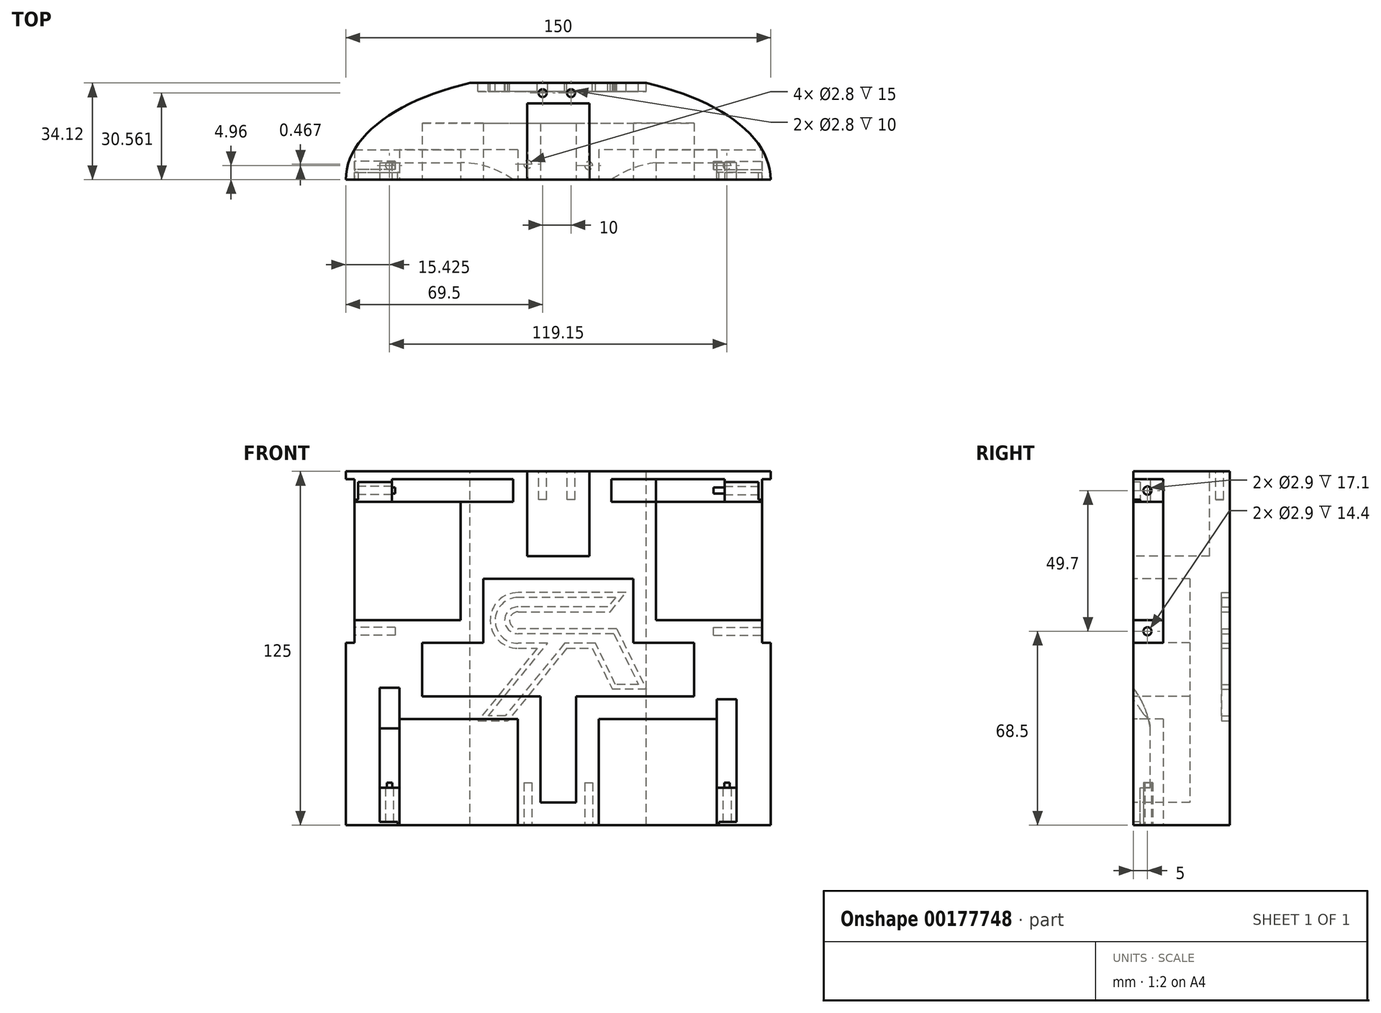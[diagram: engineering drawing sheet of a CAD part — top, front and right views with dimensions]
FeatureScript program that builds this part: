
annotation { "Feature Type Name" : "Feature", "Feature Type Description" : "" }
export const myFeature = defineFeature(function(context is Context, id is Id, definition is map)
    precondition{}
    {
        {
            var Q0;
            Q0=qCreatedBy(makeId("Top.planeOp"),FACE);
            var sketch = newSketch(context, id + "F0", { "sketchPlane" : qUnion([Q0])});
            skLineSegment(sketch, "E0.bottom", {"start": v(-150, 0) * mm, "end": v(0, 0) * mm});
            skLineSegment(sketch, "E0.top", {"start": v(-150, -75) * mm, "end": v(0, -75) * mm});
            skLineSegment(sketch, "E0.left", {"start": v(-150, 0) * mm, "end": v(-150, -75) * mm});
            skLineSegment(sketch, "E0.right", {"start": v(0, 0) * mm, "end": v(0, -75) * mm});
            skLineSegment(sketch, "E1", {"start": v(0, -37.5) * mm, "end": v(-150, -37.5) * mm});
            skPoint(sketch, "E2", {"position": v(-75, -37.5) * mm});
            skEllipse(sketch, "E3", {"center": v(-75, -37.5) * mm, "majorRadius": 75 * mm, "minorRadius": 37.5 * mm, "majorAxis": v(1, 0)});
            skSolve(sketch);
        }
        {
            var Q0;
            {var subQ0=sQuery(id+"F0.wireOp",EDGE,"E1");Q0=makeQuery(id+"F0.imprint","IMPRINT",FACE,{"disambiguationData":[TD([[makeQuery(id+"F0.imprint","IMPRINT",EDGE,{"derivedFrom":subQ0}),1.0]])]});}
            var Q1;
            {var subQ0=sQuery(id+"F0.wireOp",EDGE,"E1");Q1=makeQuery(id+"F0.imprint","IMPRINT",FACE,{"disambiguationData":[TD([[makeQuery(id+"F0.imprint","IMPRINT",EDGE,{"derivedFrom":subQ0}),-1.0]])]});}
            extrude(context, id + "F1", {"entities" : qUnion([Q0, Q1]), "depth" : 125 * mm});
        }
        {
            var Q0;
            Q0=qCreatedBy(makeId("Right.planeOp"),FACE);
            var sketch = newSketch(context, id + "F2", { "sketchPlane" : qUnion([Q0])});
            skLineSegment(sketch, "E4.bottom", {"start": v(-48.1, 114.2) * mm, "end": v(-26.9, 114.2) * mm});
            skLineSegment(sketch, "E4.top", {"start": v(-48.1, 72.5) * mm, "end": v(-26.9, 72.5) * mm});
            skLineSegment(sketch, "E4.left", {"start": v(-48.1, 114.2) * mm, "end": v(-48.1, 72.5) * mm});
            skLineSegment(sketch, "E4.right", {"start": v(-26.9, 114.2) * mm, "end": v(-26.9, 72.5) * mm});
            skPoint(sketch, "E5", {"position": v(-37.5, 125) * mm});
            skPoint(sketch, "E6", {"position": v(-37.5, 114.2) * mm});
            skLineSegment(sketch, "E7", {"start": v(-37.5, 125) * mm, "end": v(-37.5, 121.35) * mm});
            skLineSegment(sketch, "E8.bottom", {"start": v(-48.1, 113.35) * mm, "end": v(-26.9, 113.35) * mm, "construction": true});
            skLineSegment(sketch, "E8.top", {"start": v(-48.1, 73.35) * mm, "end": v(-26.9, 73.35) * mm, "construction": true});
            skLineSegment(sketch, "E8.left", {"start": v(-48.1, 113.35) * mm, "end": v(-48.1, 73.35) * mm, "construction": true});
            skLineSegment(sketch, "E8.right", {"start": v(-26.9, 113.35) * mm, "end": v(-26.9, 73.35) * mm, "construction": true});
            skPoint(sketch, "E9", {"position": v(-26.9, 93.35) * mm});
            skLineSegment(sketch, "E10.bottom", {"start": v(-48.1, 113.35) * mm, "end": v(-26.9, 113.35) * mm});
            skLineSegment(sketch, "E10.top", {"start": v(-48.1, 121.35) * mm, "end": v(-26.9, 121.35) * mm});
            skLineSegment(sketch, "E10.left", {"start": v(-48.1, 113.35) * mm, "end": v(-48.1, 121.35) * mm});
            skLineSegment(sketch, "E10.right", {"start": v(-26.9, 113.35) * mm, "end": v(-26.9, 121.35) * mm});
            skLineSegment(sketch, "E11.bottom", {"start": v(-48.1, 73.35) * mm, "end": v(-26.9, 73.35) * mm});
            skLineSegment(sketch, "E11.top", {"start": v(-48.1, 65.35) * mm, "end": v(-26.9, 65.35) * mm});
            skLineSegment(sketch, "E11.left", {"start": v(-48.1, 73.35) * mm, "end": v(-48.1, 65.35) * mm});
            skLineSegment(sketch, "E11.right", {"start": v(-26.9, 73.35) * mm, "end": v(-26.9, 65.35) * mm});
            skLineSegment(sketch, "E12", {"start": v(-37.5, 65.35) * mm, "end": v(-37.5, 0) * mm});
            skLineSegment(sketch, "E13", {"start": v(-37.5, 121.35) * mm, "end": v(-37.5, 125) * mm});
            skLineSegment(sketch, "E14.trimOffspring", {"start": v(-37.5, 114.2) * mm, "end": v(-37.5, 72.5) * mm});
            skSolve(sketch);
        }
        {
            var Q0;
            {var subQ0=sQuery(id+"F2.wireOp",EDGE,"E4.right");Q0=makeQuery(id+"F2.imprint","IMPRINT",FACE,{"disambiguationData":[TD([[makeQuery(id+"F2.imprint","IMPRINT",EDGE,{"derivedFrom":subQ0}),-1.0]])]});}
            var Q1;
            {var subQ0=sQuery(id+"F2.wireOp",EDGE,"E4.left");Q1=makeQuery(id+"F2.imprint","IMPRINT",FACE,{"disambiguationData":[TD([[makeQuery(id+"F2.imprint","IMPRINT",EDGE,{"derivedFrom":subQ0}),1.0]])]});}
            var Q2;
            {var subQ0=sQuery(id+"F2.wireOp",EDGE,"E11.left");var subQ1=sQuery(id+"F2.wireOp",EDGE,"E4.top");var subQ2=makeQuery(id+"F2.imprint","INTERSECT",VERTEX,{"derivedFrom":[subQ1,subQ0]});Q2=makeQuery(id+"F2.imprint","IMPRINT",FACE,{"disambiguationData":[TD([[makeQuery(id+"F2.imprint","IMPRINT",EDGE,{"disambiguationData":[TD([[subQ2,-1.0]])],"derivedFrom":subQ1}),1.0]])]});}
            var Q3;
            {var subQ0=sQuery(id+"F2.wireOp",EDGE,"E11.right");var subQ1=sQuery(id+"F2.wireOp",EDGE,"E4.top");var subQ2=makeQuery(id+"F2.imprint","INTERSECT",VERTEX,{"derivedFrom":[subQ1,subQ0]});Q3=makeQuery(id+"F2.imprint","IMPRINT",FACE,{"disambiguationData":[TD([[makeQuery(id+"F2.imprint","IMPRINT",EDGE,{"disambiguationData":[TD([[subQ2,1.0]])],"derivedFrom":subQ1}),1.0]])]});}
            var Q4;
            {var subQ0=sQuery(id+"F2.wireOp",EDGE,"E10.left");var subQ1=sQuery(id+"F2.wireOp",EDGE,"E4.bottom");var subQ2=makeQuery(id+"F2.imprint","INTERSECT",VERTEX,{"derivedFrom":[subQ1,subQ0]});Q4=makeQuery(id+"F2.imprint","IMPRINT",FACE,{"disambiguationData":[TD([[makeQuery(id+"F2.imprint","IMPRINT",EDGE,{"disambiguationData":[TD([[subQ2,-1.0]])],"derivedFrom":subQ1}),-1.0]])]});}
            var Q5;
            {var subQ0=sQuery(id+"F2.wireOp",EDGE,"E10.right");var subQ1=sQuery(id+"F2.wireOp",EDGE,"E4.bottom");var subQ2=makeQuery(id+"F2.imprint","INTERSECT",VERTEX,{"derivedFrom":[subQ1,subQ0]});Q5=makeQuery(id+"F2.imprint","IMPRINT",FACE,{"disambiguationData":[TD([[makeQuery(id+"F2.imprint","IMPRINT",EDGE,{"disambiguationData":[TD([[subQ2,1.0]])],"derivedFrom":subQ1}),-1.0]])]});}
            extrude(context, id + "F3", {"entities" : qUnion([Q0, Q1, Q2, Q3, Q4, Q5]), "operationType" : NewBodyOperationType.REMOVE, "oppositeDirection" : true, "depth" : 155.5 * mm});
        }
        {
            var Q0;
            Q0=makeQuery(id+"F3.boolean.opBoolean","COPY",FACE,{"derivedFrom":makeQuery(id+"F3.opExtrude","SWEPT_FACE",FACE,{"disambiguationData":[OSD([sQuery(id+"F2.wireOp",EDGE,"E4.top")])]})});
            var sketch = newSketch(context, id + "F4", { "sketchPlane" : qUnion([Q0])});
            skLineSegment(sketch, "E15", {"start": v(-3.06, -48.1) * mm, "end": v(-3.06, -26.9) * mm});
            skEllipticalArc(sketch, "E16.0", {});
            skLineSegment(sketch, "E17", {"start": v(-146.94, -48.1) * mm, "end": v(-146.94, -26.9) * mm});
            skEllipticalArc(sketch, "E18.0", {});
            const initialGuessF4  = {"E16.0": [-0.075, -0.0375, 1, 0, 0.075, 0.0375, 5.996612290444908, 0.28657301673467844], "E18.0": [-0.075, -0.0375, 1, 0, 0.075, 0.0375, 2.855019636855115, 3.428165670324471]};
            skSetInitialGuess(sketch, initialGuessF4);
            skSolve(sketch);
        }
        {
            var Q0;
            Q0=makeQuery(id+"F4.imprint","IMPRINT",FACE,{"disambiguationData":[TD([[makeQuery(id+"F4.imprint","IMPRINT",EDGE,{"derivedFrom":sQuery(id+"F4.wireOp",EDGE,"E17")}),1.0]])]});
            var Q1;
            Q1=makeQuery(id+"F4.imprint","IMPRINT",FACE,{"disambiguationData":[TD([[makeQuery(id+"F4.imprint","IMPRINT",EDGE,{"derivedFrom":sQuery(id+"F4.wireOp",EDGE,"E15")}),-1.0]])]});
            extrude(context, id + "F5", {"entities" : qUnion([Q0, Q1]), "operationType" : NewBodyOperationType.REMOVE, "oppositeDirection" : true, "depth" : 8 * mm});
        }
        {
            var Q0;
            Q0=makeQuery(id+"F3.boolean.opBoolean","COPY",FACE,{"derivedFrom":makeQuery(id+"F3.opExtrude","SWEPT_FACE",FACE,{"disambiguationData":[OSD([sQuery(id+"F2.wireOp",EDGE,"E4.bottom")])]})});
            var sketch = newSketch(context, id + "F6", { "sketchPlane" : qUnion([Q0])});
            skLineSegment(sketch, "E19", {"start": v(-3.06, 26.9) * mm, "end": v(-3.06, 48.1) * mm});
            skEllipticalArc(sketch, "E20.0", {});
            skLineSegment(sketch, "E21", {"start": v(-146.94, 26.9) * mm, "end": v(-146.94, 48.1) * mm});
            skEllipticalArc(sketch, "E22.0", {});
            const initialGuessF6  = {"E20.0": [-0.075, 0.0375, 1, 0, 0.075, 0.0375, 5.996612290444908, 0.28657301673467805], "E22.0": [-0.075, 0.0375, 1, 0, 0.075, 0.0375, 2.8550196368551153, 3.428165670324471]};
            skSetInitialGuess(sketch, initialGuessF6);
            skSolve(sketch);
        }
        {
            var Q0;
            Q0=makeQuery(id+"F6.imprint","IMPRINT",FACE,{"disambiguationData":[TD([[makeQuery(id+"F6.imprint","IMPRINT",EDGE,{"derivedFrom":sQuery(id+"F6.wireOp",EDGE,"E21")}),1.0]])]});
            var Q1;
            Q1=makeQuery(id+"F6.imprint","IMPRINT",FACE,{"disambiguationData":[TD([[makeQuery(id+"F6.imprint","IMPRINT",EDGE,{"derivedFrom":sQuery(id+"F6.wireOp",EDGE,"E19")}),-1.0]])]});
            extrude(context, id + "F7", {"entities" : qUnion([Q0, Q1]), "operationType" : NewBodyOperationType.REMOVE, "oppositeDirection" : true, "depth" : 8 * mm});
        }
        {
            var Q0;
            Q0=makeQuery(id+"F3.boolean.opBoolean","COPY",FACE,{"derivedFrom":makeQuery(id+"F3.opExtrude","SWEPT_FACE",FACE,{"disambiguationData":[OSD([sQuery(id+"F2.wireOp",EDGE,"E4.top")])]})});
            var sketch = newSketch(context, id + "F8", { "sketchPlane" : qUnion([Q0])});
            skLineSegment(sketch, "E23.bottom", {"start": v(-109.44, -26.9) * mm, "end": v(-40.56, -26.9) * mm});
            skLineSegment(sketch, "E23.top", {"start": v(-109.44, -48.1) * mm, "end": v(-40.56, -48.1) * mm});
            skLineSegment(sketch, "E23.left", {"start": v(-109.44, -26.9) * mm, "end": v(-109.44, -48.1) * mm});
            skLineSegment(sketch, "E23.right", {"start": v(-40.56, -26.9) * mm, "end": v(-40.56, -48.1) * mm});
            skSolve(sketch);
        }
        {
            var Q0;
            Q0=makeQuery(id+"F8.imprint","IMPRINT",FACE,{"disambiguationData":[TD([[makeQuery(id+"F8.imprint","IMPRINT",EDGE,{"derivedFrom":sQuery(id+"F8.wireOp",EDGE,"E23.bottom")}),-1.0]])]});
            extrude(context, id + "F9", {"entities" : qUnion([Q0]), "operationType" : NewBodyOperationType.ADD, "depth" : 46 * mm});
        }
        {
            var Q0;
            Q0=makeQuery(id+"F9.boolean.opBoolean","SPLIT",FACE,{"disambiguationData":[TD([makeQuery(id+"F7.boolean.opBoolean","COPY",FACE,{"derivedFrom":makeQuery(id+"F7.opExtrude","SWEPT_FACE",FACE,{"disambiguationData":[OSD([sQuery(id+"F6.wireOp",EDGE,"E21")])]})})])],"derivedFrom":makeQuery(id+"F3.boolean.opBoolean","COPY",FACE,{"derivedFrom":makeQuery(id+"F3.opExtrude","SWEPT_FACE",FACE,{"disambiguationData":[OSD([sQuery(id+"F2.wireOp",EDGE,"E4.bottom")])]})})});
            var sketch = newSketch(context, id + "F10", { "sketchPlane" : qUnion([Q0])});
            skLineSegment(sketch, "E24", {"start": v(-145.7, 26.9) * mm, "end": v(-145.7, 48.1) * mm, "construction": true});
            skLineSegment(sketch, "E25", {"start": v(-145.7, 37.5) * mm, "end": v(-142.91, 37.5) * mm});
            skLineSegment(sketch, "E26.bottom", {"start": v(-145.7, 35) * mm, "end": v(-4.3, 35) * mm});
            skLineSegment(sketch, "E26.top", {"start": v(-145.7, 40) * mm, "end": v(-4.3, 40) * mm});
            skLineSegment(sketch, "E26.left", {"start": v(-145.7, 35) * mm, "end": v(-145.7, 40) * mm});
            skLineSegment(sketch, "E26.right", {"start": v(-4.3, 35) * mm, "end": v(-4.3, 40) * mm});
            skLineSegment(sketch, "E27", {"start": v(-4.3, 26.9) * mm, "end": v(-4.3, 48.1) * mm, "construction": true});
            skLineSegment(sketch, "E28", {"start": v(-145.7, 37.5) * mm, "end": v(-145.7, 40) * mm});
            skLineSegment(sketch, "E29", {"start": v(-145.7, 35) * mm, "end": v(-145.7, 37.5) * mm});
            skSolve(sketch);
        }
        {
            var Q0;
            Q0=qSketchRegion(id+"F10",true);
            extrude(context, id + "F11", {"entities" : qUnion([Q0]), "operationType" : NewBodyOperationType.REMOVE, "oppositeDirection" : true, "depth" : 7 * mm});
        }
        {
            var Q0;
            Q0=makeQuery(id+"F9.boolean.opBoolean","SPLIT",FACE,{"disambiguationData":[TD([makeQuery(id+"F7.boolean.opBoolean","COPY",FACE,{"derivedFrom":makeQuery(id+"F7.opExtrude","SWEPT_FACE",FACE,{"disambiguationData":[OSD([sQuery(id+"F6.wireOp",EDGE,"E21")])]})})])],"derivedFrom":makeQuery(id+"F3.boolean.opBoolean","COPY",FACE,{"derivedFrom":makeQuery(id+"F3.opExtrude","SWEPT_FACE",FACE,{"disambiguationData":[OSD([sQuery(id+"F2.wireOp",EDGE,"E4.bottom")])]})})});
            var sketch = newSketch(context, id + "F12", { "sketchPlane" : qUnion([Q0])});
            skLineSegment(sketch, "E30.bottom", {"start": v(-133.7, 31.5) * mm, "end": v(-16.3, 31.5) * mm});
            skLineSegment(sketch, "E30.top", {"start": v(-133.7, 43.5) * mm, "end": v(-16.3, 43.5) * mm});
            skLineSegment(sketch, "E30.left", {"start": v(-133.7, 31.5) * mm, "end": v(-133.7, 43.5) * mm});
            skLineSegment(sketch, "E30.right", {"start": v(-16.3, 31.5) * mm, "end": v(-16.3, 43.5) * mm});
            skLineSegment(sketch, "E31", {"start": v(-133.7, 35) * mm, "end": v(-133.7, 40) * mm});
            skPoint(sketch, "E32", {"position": v(-133.7, 37.5) * mm});
            skLineSegment(sketch, "E33", {"start": v(-16.3, 35) * mm, "end": v(-16.3, 40) * mm});
            skPoint(sketch, "E34", {"position": v(-16.3, 37.5) * mm});
            skSolve(sketch);
        }
        {
            var Q0;
            Q0=qSketchRegion(id+"F12",true);
            extrude(context, id + "F13", {"entities" : qUnion([Q0]), "operationType" : NewBodyOperationType.REMOVE, "oppositeDirection" : true, "depth" : 8 * mm});
        }
        {
            var Q0;
            Q0=makeQuery(id+"F9.boolean.opBoolean","SPLIT",FACE,{"disambiguationData":[TD([makeQuery(id+"F7.boolean.opBoolean","COPY",FACE,{"derivedFrom":makeQuery(id+"F7.opExtrude","SWEPT_FACE",FACE,{"disambiguationData":[OSD([sQuery(id+"F6.wireOp",EDGE,"E21")])]})})])],"derivedFrom":makeQuery(id+"F3.boolean.opBoolean","COPY",FACE,{"derivedFrom":makeQuery(id+"F3.opExtrude","SWEPT_FACE",FACE,{"disambiguationData":[OSD([sQuery(id+"F2.wireOp",EDGE,"E4.bottom")])]})})});
            var sketch = newSketch(context, id + "F14", { "sketchPlane" : qUnion([Q0])});
            skArc(sketch, "E35", {"start": v(-109.44, 31.5) * mm, "mid": v(-83.34, 45.45) * mm, "end": v(-80.45, 74.9) * mm});
            skArc(sketch, "E36", {"start": v(-109.44, 43.5) * mm, "mid": v(-91.99, 53.74) * mm, "end": v(-92.41, 73.98) * mm});
            skEllipticalArc(sketch, "E37.0", {});
            skLineSegment(sketch, "E38", {"start": v(-109.44, 31.5) * mm, "end": v(-109.44, 43.5) * mm});
            skArc(sketch, "E39", {"start": v(-69.55, 74.9) * mm, "mid": v(-65.03, 46.53) * mm, "end": v(-40.56, 31.5) * mm});
            skArc(sketch, "E40", {"start": v(-57.59, 73.98) * mm, "mid": v(-55.43, 55.19) * mm, "end": v(-40.56, 43.5) * mm});
            skEllipticalArc(sketch, "E41.0", {});
            skLineSegment(sketch, "E42", {"start": v(-40.56, 31.5) * mm, "end": v(-40.56, 43.5) * mm});
            skLineSegment(sketch, "E43", {"start": v(-75, 37.5) * mm, "end": v(-75, 74.9) * mm, "construction": true});
            skLineSegment(sketch, "E44", {"start": v(-69.55, 74.9) * mm, "end": v(-75, 74.9) * mm, "construction": true});
            skLineSegment(sketch, "E45", {"start": v(-80.45, 74.9) * mm, "end": v(-75, 74.9) * mm, "construction": true});
            const initialGuessF14  = {"E37.0": [-0.075, 0.0375, 1, 0, 0.075, 0.0375, 1.6434997456011395, 1.8050969396186902], "E41.0": [-0.075, 0.0375, 1, 0, 0.075, 0.0375, 1.3364957139711027, 1.4980929079886538], "E37.0": [-0.075, 0.0375, 1, 0, 0.075, 0.0375, 1.6434997456011395, 1.8050969396186902]};
            skSetInitialGuess(sketch, initialGuessF14);
            skSolve(sketch);
        }
        {
            var Q0;
            Q0=qSketchRegion(id+"F14",true);
            extrude(context, id + "F15", {"entities" : qUnion([Q0]), "operationType" : NewBodyOperationType.REMOVE, "oppositeDirection" : true, "depth" : 8 * mm});
        }
        {
            var Q0;
            Q0=makeQuery(id+"F15.boolean.opBoolean","MERGE",FACE,{"derivedFrom":[makeQuery(id+"F13.boolean.opBoolean","MERGE",FACE,{"derivedFrom":[makeQuery(id+"F11.boolean.opBoolean","COPY",FACE,{"derivedFrom":makeQuery(id+"F11.opExtrude","CAP_FACE",FACE,{"disambiguationData":[OSD([sQuery(id+"F10.wireOp",EDGE,"E26.bottom"),sQuery(id+"F10.wireOp",EDGE,"E26.top"),sQuery(id+"F10.wireOp",EDGE,"E26.right"),sQuery(id+"F10.wireOp",EDGE,"E28"),sQuery(id+"F10.wireOp",EDGE,"E29")])],"isStart":true})}),makeQuery(id+"F13.opExtrude","CAP_FACE",FACE,{"disambiguationData":[OSD([sQuery(id+"F12.wireOp",EDGE,"E30.bottom"),sQuery(id+"F12.wireOp",EDGE,"E30.top"),sQuery(id+"F12.wireOp",EDGE,"E30.left"),sQuery(id+"F12.wireOp",EDGE,"E30.right"),sQuery(id+"F12.wireOp",EDGE,"E31"),sQuery(id+"F12.wireOp",EDGE,"E33")])],"isStart":true})]}),makeQuery(id+"F15.opExtrude","CAP_FACE",FACE,{"disambiguationData":[OSD([sQuery(id+"F14.wireOp",EDGE,"E35"),sQuery(id+"F14.wireOp",EDGE,"E36"),sQuery(id+"F14.wireOp",EDGE,"E38"),sQuery(id+"F14.wireOp",EDGE,"E37.0")])],"isStart":true}),makeQuery(id+"F15.opExtrude","CAP_FACE",FACE,{"disambiguationData":[OSD([sQuery(id+"F14.wireOp",EDGE,"E39"),sQuery(id+"F14.wireOp",EDGE,"E40"),sQuery(id+"F14.wireOp",EDGE,"E41.0"),sQuery(id+"F14.wireOp",EDGE,"E42")])],"isStart":true})]});
            var sketch = newSketch(context, id + "F16", { "sketchPlane" : qUnion([Q0])});
            skArc(sketch, "E46.0", {"start": v(-84.76, -43.5) * mm, "mid": v(-78.35, -58.62) * mm, "end": v(-80.45, -74.9) * mm, "construction": true});
            skArc(sketch, "E46.1", {"start": v(-69.55, -74.9) * mm, "mid": v(-70.05, -58.36) * mm, "end": v(-62.76, -43.5) * mm, "construction": true});
            skLineSegment(sketch, "E47", {"start": v(-62.76, -43.5) * mm, "end": v(-84.76, -43.5) * mm});
            skArc(sketch, "E48", {"start": v(-84.76, -43.5) * mm, "mid": v(-95.72, -34.66) * mm, "end": v(-109.44, -31.5) * mm});
            skArc(sketch, "E49", {"start": v(-40.56, -31.5) * mm, "mid": v(-52.8, -35.39) * mm, "end": v(-62.76, -43.5) * mm});
            skLineSegment(sketch, "E50", {"start": v(-109.44, -31.5) * mm, "end": v(-40.56, -31.5) * mm});
            skSolve(sketch);
        }
        {
            var Q0;
            Q0=qSketchRegion(id+"F16",true);
            extrude(context, id + "F17", {"entities" : qUnion([Q0]), "operationType" : NewBodyOperationType.ADD, "depth" : 9.4 * mm});
        }
        {
            var Q0;
            Q0=makeQuery(id+"F7.boolean.opBoolean","COPY",FACE,{"derivedFrom":makeQuery(id+"F7.opExtrude","SWEPT_FACE",FACE,{"disambiguationData":[OSD([sQuery(id+"F6.wireOp",EDGE,"E19")])]})});
            var sketch = newSketch(context, id + "F18", { "sketchPlane" : qUnion([Q0])});
            skLineSegment(sketch, "E51", {"start": v(-48.1, 118.2) * mm, "end": v(-26.9, 118.2) * mm, "construction": true});
            skCircle(sketch, "E52", {"center": v(-42.5, 118.2) * mm, "radius": 1.45 * mm});
            skCircle(sketch, "E53", {"center": v(-32.5, 118.2) * mm, "radius": 1.45 * mm});
            skLineSegment(sketch, "E54", {"start": v(-32.5, 118.2) * mm, "end": v(-42.5, 118.2) * mm});
            skPoint(sketch, "E55", {"position": v(-37.5, 118.2) * mm});
            skLineSegment(sketch, "E56", {"start": v(-26.9, 68.5) * mm, "end": v(-48.1, 68.5) * mm, "construction": true});
            skCircle(sketch, "E57", {"center": v(-32.5, 68.5) * mm, "radius": 1.45 * mm});
            skCircle(sketch, "E58", {"center": v(-42.5, 68.5) * mm, "radius": 1.45 * mm});
            skPoint(sketch, "E59", {"position": v(-37.5, 68.5) * mm});
            skLineSegment(sketch, "E60", {"start": v(-32.5, 68.5) * mm, "end": v(-42.5, 68.5) * mm});
            skSolve(sketch);
        }
        {
            var Q0;
            Q0=qSketchRegion(id+"F18",true);
            extrude(context, id + "F19", {"entities" : qUnion([Q0]), "operationType" : NewBodyOperationType.REMOVE, "oppositeDirection" : true, "depth" : 17.1 * mm});
        }
        {
            var Q0;
            Q0=makeQuery(id+"F7.boolean.opBoolean","COPY",FACE,{"derivedFrom":makeQuery(id+"F7.opExtrude","SWEPT_FACE",FACE,{"disambiguationData":[OSD([sQuery(id+"F6.wireOp",EDGE,"E21")])]})});
            var sketch = newSketch(context, id + "F20", { "sketchPlane" : qUnion([Q0])});
            skCircle(sketch, "E61.0", {"center": v(32.5, 68.5) * mm, "radius": 1.45 * mm});
            skCircle(sketch, "E61.1", {"center": v(42.5, 68.5) * mm, "radius": 1.45 * mm});
            skCircle(sketch, "E61.2", {"center": v(42.5, 118.2) * mm, "radius": 1.45 * mm});
            skCircle(sketch, "E61.3", {"center": v(32.5, 118.2) * mm, "radius": 1.45 * mm});
            skSolve(sketch);
        }
        {
            var Q0;
            Q0=qSketchRegion(id+"F20",true);
            extrude(context, id + "F21", {"entities" : qUnion([Q0]), "operationType" : NewBodyOperationType.REMOVE, "oppositeDirection" : true, "depth" : 14.4 * mm});
        }
        {
            var Q0;
            Q0=makeQuery(id+"F1.opExtrude","CAP_FACE",FACE,{"disambiguationData":[OSD([sQuery(id+"F0.wireOp",EDGE,"E3")])],"isStart":true});
            var sketch = newSketch(context, id + "F22", { "sketchPlane" : qUnion([Q0])});
            skLineSegment(sketch, "E62", {"start": v(-75, 0) * mm, "end": v(-75, 75) * mm, "construction": true});
            skLineSegment(sketch, "E63.bottom", {"start": v(-19, 26.9) * mm, "end": v(-60.7, 26.9) * mm});
            skLineSegment(sketch, "E63.top", {"start": v(-19, 48.1) * mm, "end": v(-60.7, 48.1) * mm});
            skLineSegment(sketch, "E63.left", {"start": v(-19, 26.9) * mm, "end": v(-19, 48.1) * mm});
            skLineSegment(sketch, "E63.right", {"start": v(-60.7, 26.9) * mm, "end": v(-60.7, 48.1) * mm});
            skLineSegment(sketch, "E64.bottom", {"start": v(-89.3, 26.9) * mm, "end": v(-131, 26.9) * mm});
            skLineSegment(sketch, "E64.top", {"start": v(-89.3, 48.1) * mm, "end": v(-131, 48.1) * mm});
            skLineSegment(sketch, "E64.left", {"start": v(-89.3, 26.9) * mm, "end": v(-89.3, 48.1) * mm});
            skLineSegment(sketch, "E64.right", {"start": v(-131, 26.9) * mm, "end": v(-131, 48.1) * mm});
            skLineSegment(sketch, "E65", {"start": v(-89.3, 37.5) * mm, "end": v(-75, 37.5) * mm});
            skLineSegment(sketch, "E66", {"start": v(-75, 37.5) * mm, "end": v(-60.7, 37.5) * mm});
            skLineSegment(sketch, "E67", {"start": v(-60.7, 37.5) * mm, "end": v(-75, 37.5) * mm, "construction": true});
            skLineSegment(sketch, "E68", {"start": v(-89.3, 37.5) * mm, "end": v(-75, 37.5) * mm, "construction": true});
            skLineSegment(sketch, "E69.bottom", {"start": v(-19.85, 26.9) * mm, "end": v(-59.85, 26.9) * mm});
            skLineSegment(sketch, "E69.top", {"start": v(-19.85, 48.1) * mm, "end": v(-59.85, 48.1) * mm});
            skPoint(sketch, "E70", {"position": v(-39.85, 26.9) * mm});
            skLineSegment(sketch, "E71.bottom", {"start": v(-19.85, 26.9) * mm, "end": v(-11.85, 26.9) * mm});
            skLineSegment(sketch, "E71.top", {"start": v(-19.85, 48.1) * mm, "end": v(-11.85, 48.1) * mm});
            skLineSegment(sketch, "E71.right", {"start": v(-11.85, 26.9) * mm, "end": v(-11.85, 48.1) * mm});
            skLineSegment(sketch, "E72.bottom", {"start": v(-60.7, 48.1) * mm, "end": v(-67.85, 48.1) * mm});
            skLineSegment(sketch, "E72.top", {"start": v(-60.7, 26.9) * mm, "end": v(-67.85, 26.9) * mm});
            skLineSegment(sketch, "E72.left", {"start": v(-60.7, 48.1) * mm, "end": v(-60.7, 26.9) * mm});
            skLineSegment(sketch, "E72.right", {"start": v(-67.85, 48.1) * mm, "end": v(-67.85, 26.9) * mm});
            skPoint(sketch, "E73.oppositeSnap0", {"position": v(-82.15, 37.5) * mm});
            skLineSegment(sketch, "E73.bottom", {"start": v(-89.3, 26.9) * mm, "end": v(-82.15, 26.9) * mm});
            skLineSegment(sketch, "E73.top", {"start": v(-89.3, 48.1) * mm, "end": v(-82.15, 48.1) * mm});
            skLineSegment(sketch, "E73.right", {"start": v(-82.15, 26.9) * mm, "end": v(-82.15, 48.1) * mm});
            skLineSegment(sketch, "E74.bottom", {"start": v(-131, 26.9) * mm, "end": v(-138.15, 26.9) * mm});
            skLineSegment(sketch, "E74.top", {"start": v(-131, 48.1) * mm, "end": v(-138.15, 48.1) * mm});
            skLineSegment(sketch, "E74.right", {"start": v(-138.15, 26.9) * mm, "end": v(-138.15, 48.1) * mm});
            skLineSegment(sketch, "E75.bottom", {"start": v(-90.15, 26.9) * mm, "end": v(-130.15, 26.9) * mm});
            skLineSegment(sketch, "E75.top", {"start": v(-90.15, 48.1) * mm, "end": v(-130.15, 48.1) * mm});
            skPoint(sketch, "E76", {"position": v(-110.15, 26.9) * mm});
            skPoint(sketch, "E77", {"position": v(-67.85, 37.5) * mm});
            skLineSegment(sketch, "E78", {"start": v(-19, 26.9) * mm, "end": v(-11.85, 26.9) * mm});
            skLineSegment(sketch, "E79", {"start": v(-19, 48.1) * mm, "end": v(-11.85, 48.1) * mm});
            skCircle(sketch, "E80", {"center": v(-15.42, 32.53) * mm, "radius": 1.4 * mm});
            skCircle(sketch, "E81", {"center": v(-15.42, 42.53) * mm, "radius": 1.4 * mm});
            skCircle(sketch, "E82", {"center": v(-64.27, 32.54) * mm, "radius": 1.4 * mm});
            skCircle(sketch, "E83", {"center": v(-64.27, 42.54) * mm, "radius": 1.4 * mm});
            skCircle(sketch, "E84", {"center": v(-85.73, 42.07) * mm, "radius": 1.4 * mm});
            skCircle(sketch, "E85", {"center": v(-85.73, 32.07) * mm, "radius": 1.4 * mm});
            skCircle(sketch, "E86", {"center": v(-134.57, 32.51) * mm, "radius": 1.4 * mm});
            skCircle(sketch, "E87", {"center": v(-134.57, 42.51) * mm, "radius": 1.4 * mm});
            skLineSegment(sketch, "E88", {"start": v(-138.15, 37.5) * mm, "end": v(-11.85, 37.5) * mm, "construction": true});
            skLineSegment(sketch, "E89", {"start": v(-15.42, 32.53) * mm, "end": v(-15.42, 42.53) * mm});
            skLineSegment(sketch, "E90", {"start": v(-64.27, 32.54) * mm, "end": v(-64.27, 42.54) * mm});
            skLineSegment(sketch, "E91", {"start": v(-85.73, 32.07) * mm, "end": v(-85.73, 42.07) * mm});
            skLineSegment(sketch, "E92", {"start": v(-134.57, 32.51) * mm, "end": v(-134.57, 42.51) * mm});
            skSolve(sketch);
        }
        {
            var Q0;
            {var subQ0=sQuery(id+"F22.wireOp",EDGE,"E63.left");Q0=makeQuery(id+"F22.imprint","IMPRINT",FACE,{"disambiguationData":[TD([[makeQuery(id+"F22.imprint","IMPRINT",EDGE,{"derivedFrom":subQ0}),1.0]])]});}
            var Q1;
            {var subQ1=sQuery(id+"F22.wireOp",EDGE,"E63.bottom");Q1=makeQuery(id+"F22.imprint","IMPRINT",FACE,{"disambiguationData":[TD([[makeQuery(id+"F22.imprint","IMPRINT",EDGE,{"derivedFrom":subQ1}),-1.0]])]});}
            var Q2;
            {var subQ0=sQuery(id+"F22.wireOp",EDGE,"E64.right");Q2=makeQuery(id+"F22.imprint","IMPRINT",FACE,{"disambiguationData":[TD([[makeQuery(id+"F22.imprint","IMPRINT",EDGE,{"derivedFrom":subQ0}),-1.0]])]});}
            extrude(context, id + "F23", {"entities" : qUnion([Q0, Q1, Q2]), "operationType" : NewBodyOperationType.REMOVE, "oppositeDirection" : true, "depth" : 37.5 * mm});
        }
        {
            var Q0;
            Q0=makeQuery(id+"F22.imprint","IMPRINT",FACE,{"disambiguationData":[TD([[makeQuery(id+"F22.imprint","IMPRINT",EDGE,{"derivedFrom":sQuery(id+"F22.wireOp",EDGE,"E80")}),1.0]])]});
            var Q1;
            Q1=makeQuery(id+"F22.imprint","IMPRINT",FACE,{"disambiguationData":[TD([[makeQuery(id+"F22.imprint","IMPRINT",EDGE,{"derivedFrom":sQuery(id+"F22.wireOp",EDGE,"E81")}),1.0]])]});
            var Q2;
            Q2=makeQuery(id+"F22.imprint","IMPRINT",FACE,{"disambiguationData":[TD([[makeQuery(id+"F22.imprint","IMPRINT",EDGE,{"derivedFrom":sQuery(id+"F22.wireOp",EDGE,"E82")}),1.0]])]});
            var Q3;
            Q3=makeQuery(id+"F22.imprint","IMPRINT",FACE,{"disambiguationData":[TD([[makeQuery(id+"F22.imprint","IMPRINT",EDGE,{"derivedFrom":sQuery(id+"F22.wireOp",EDGE,"E83")}),1.0]])]});
            var Q4;
            Q4=makeQuery(id+"F22.imprint","IMPRINT",FACE,{"disambiguationData":[TD([[makeQuery(id+"F22.imprint","IMPRINT",EDGE,{"derivedFrom":sQuery(id+"F22.wireOp",EDGE,"E85")}),1.0]])]});
            var Q5;
            Q5=makeQuery(id+"F22.imprint","IMPRINT",FACE,{"disambiguationData":[TD([[makeQuery(id+"F22.imprint","IMPRINT",EDGE,{"derivedFrom":sQuery(id+"F22.wireOp",EDGE,"E84")}),1.0]])]});
            var Q6;
            Q6=makeQuery(id+"F22.imprint","IMPRINT",FACE,{"disambiguationData":[TD([[makeQuery(id+"F22.imprint","IMPRINT",EDGE,{"derivedFrom":sQuery(id+"F22.wireOp",EDGE,"E86")}),1.0]])]});
            var Q7;
            Q7=makeQuery(id+"F22.imprint","IMPRINT",FACE,{"disambiguationData":[TD([[makeQuery(id+"F22.imprint","IMPRINT",EDGE,{"derivedFrom":sQuery(id+"F22.wireOp",EDGE,"E87")}),1.0]])]});
            extrude(context, id + "F24", {"entities" : qUnion([Q0, Q1, Q2, Q3, Q4, Q5, Q6, Q7]), "operationType" : NewBodyOperationType.REMOVE, "oppositeDirection" : true, "depth" : 15 * mm});
        }
        {
            var Q0;
            Q0=makeQuery(id+"F23.boolean.opBoolean","COPY",FACE,{"derivedFrom":makeQuery(id+"F23.opExtrude","SWEPT_FACE",FACE,{"disambiguationData":[OSD([sQuery(id+"F22.wireOp",EDGE,"E64.right")])]})});
            var sketch = newSketch(context, id + "F25", { "sketchPlane" : qUnion([Q0])});
            skLineSegment(sketch, "E93.bottom", {"start": v(-35, 1.25) * mm, "end": v(-40, 1.25) * mm});
            skLineSegment(sketch, "E93.left", {"start": v(-35, 1.25) * mm, "end": v(-35, 13.25) * mm});
            skLineSegment(sketch, "E93.right", {"start": v(-40, 1.25) * mm, "end": v(-40, 13.25) * mm});
            skLineSegment(sketch, "E94", {"start": v(-37.5, 0) * mm, "end": v(-37.5, 13.25) * mm, "construction": true});
            skLineSegment(sketch, "E95", {"start": v(-37.5, 1.25) * mm, "end": v(-35, 1.25) * mm});
            skPoint(sketch, "E95.startSnap0", {"position": v(-37.5, 1.25) * mm});
            skLineSegment(sketch, "E96", {"start": v(-37.5, 1.25) * mm, "end": v(-40, 1.25) * mm});
            skPoint(sketch, "E97", {"position": v(-37.5, 31.05) * mm});
            skLineSegment(sketch, "E98.bottom", {"start": v(-31.5, 13.25) * mm, "end": v(-35, 13.25) * mm});
            skLineSegment(sketch, "E98.left", {"start": v(-31.5, 13.25) * mm, "end": v(-31.5, 34.22) * mm});
            skLineSegment(sketch, "E98.right", {"start": v(-43.5, 13.25) * mm, "end": v(-43.5, 34.22) * mm});
            skPoint(sketch, "E99.trimOffspring.end.orphan", {"position": v(-37.5, 32.45) * mm});
            skPoint(sketch, "E100.start.orphan", {"position": v(-40, 31.05) * mm});
            skPoint(sketch, "E93.top.start.orphan", {"position": v(-35, 31.05) * mm});
            skLineSegment(sketch, "E101.trimOffspring", {"start": v(-40, 13.25) * mm, "end": v(-43.5, 13.25) * mm});
            skLineSegment(sketch, "E102", {"start": v(-40, 13.25) * mm, "end": v(-35, 13.25) * mm});
            skLineSegment(sketch, "E103", {"start": v(-43.5, 13.25) * mm, "end": v(-31.5, 13.25) * mm});
            skLineSegment(sketch, "E104", {"start": v(-37.5, 34.22) * mm, "end": v(-37.5, 13.25) * mm});
            skArc(sketch, "E105", {"start": v(-43.5, 34.22) * mm, "mid": v(-54.18, 46.6) * mm, "end": v(-70.51, 47.22) * mm});
            skArc(sketch, "E106", {"start": v(-31.5, 34.22) * mm, "mid": v(-45.26, 55.7) * mm, "end": v(-70.51, 59.22) * mm});
            skLineSegment(sketch, "E107", {"start": v(-43.5, 34.22) * mm, "end": v(-31.5, 34.22) * mm});
            skLineSegment(sketch, "E108", {"start": v(-70.51, 59.22) * mm, "end": v(-70.51, 47.22) * mm});
            skPoint(sketch, "E109.orphan", {"position": v(-31.5, 37.5) * mm});
            skPoint(sketch, "E110.orphan", {"position": v(-37.5, 37.5) * mm});
            skPoint(sketch, "E98.top.end.orphan", {"position": v(-43.5, 37.5) * mm});
            skSolve(sketch);
        }
        {
            var Q0;
            Q0=qSketchRegion(id+"F25",true);
            extrude(context, id + "F26", {"entities" : qUnion([Q0]), "operationType" : NewBodyOperationType.REMOVE, "oppositeDirection" : true, "depth" : 7 * mm});
        }
        {
            var Q0;
            Q0=makeQuery(id+"F23.boolean.opBoolean","COPY",FACE,{"derivedFrom":makeQuery(id+"F23.opExtrude","SWEPT_FACE",FACE,{"disambiguationData":[OSD([sQuery(id+"F22.wireOp",EDGE,"E63.left")])]})});
            var sketch = newSketch(context, id + "F27", { "sketchPlane" : qUnion([Q0])});
            skLineSegment(sketch, "E111.0.2", {"start": v(43.5, 34.22) * mm, "end": v(43.5, 13.25) * mm});
            skLineSegment(sketch, "E111.0.3", {"start": v(43.5, 13.25) * mm, "end": v(40, 13.25) * mm});
            skLineSegment(sketch, "E111.0.4", {"start": v(40, 13.25) * mm, "end": v(40, 1.25) * mm});
            skLineSegment(sketch, "E111.0.5", {"start": v(40, 1.25) * mm, "end": v(35, 1.25) * mm});
            skLineSegment(sketch, "E111.0.6", {"start": v(35, 1.25) * mm, "end": v(35, 13.25) * mm});
            skLineSegment(sketch, "E111.0.7", {"start": v(35, 13.25) * mm, "end": v(31.5, 13.25) * mm});
            skLineSegment(sketch, "E111.0.8", {"start": v(31.5, 13.25) * mm, "end": v(31.5, 34.22) * mm});
            skLineSegment(sketch, "E112", {"start": v(57.85, 60.27) * mm, "end": v(57.85, 47.95) * mm});
            skArc(sketch, "E113", {"start": v(57.85, 60.27) * mm, "mid": v(39.24, 52.75) * mm, "end": v(31.5, 34.22) * mm});
            skArc(sketch, "E114", {"start": v(57.85, 47.95) * mm, "mid": v(47.74, 44.15) * mm, "end": v(43.5, 34.22) * mm});
            skSolve(sketch);
        }
        {
            var Q0;
            {var subQ0=sQuery(id+"F27.wireOp",EDGE,"E111.0.2");Q0=makeQuery(id+"F27.imprint","IMPRINT",FACE,{"disambiguationData":[TD([[makeQuery(id+"F27.imprint","IMPRINT",EDGE,{"derivedFrom":subQ0}),-1.0]])]});}
            extrude(context, id + "F28", {"entities" : qUnion([Q0]), "operationType" : NewBodyOperationType.REMOVE, "oppositeDirection" : true, "depth" : 7 * mm});
        }
        {
            var Q0;
            Q0=makeQuery(id+"F23.boolean.opBoolean","COPY",FACE,{"derivedFrom":makeQuery(id+"F23.opExtrude","SWEPT_FACE",FACE,{"disambiguationData":[OSD([sQuery(id+"F22.wireOp",EDGE,"E63.left")])]})});
            var sketch = newSketch(context, id + "F29", { "sketchPlane" : qUnion([Q0])});
            skArc(sketch, "E115", {"start": v(80.51, 59.28) * mm, "mid": v(51.36, 55.84) * mm, "end": v(31.5, 34.22) * mm});
            skArc(sketch, "E116", {"start": v(82.64, 47.28) * mm, "mid": v(60.63, 48.07) * mm, "end": v(43.5, 34.22) * mm});
            skLineSegment(sketch, "E117", {"start": v(80.51, 59.28) * mm, "end": v(82.64, 47.28) * mm});
            skPoint(sketch, "E118.0", {"position": v(31.5, 34.22) * mm});
            skPoint(sketch, "E118.1", {"position": v(43.5, 34.22) * mm});
            skLineSegment(sketch, "E119", {"start": v(31.5, 34.22) * mm, "end": v(43.5, 34.22) * mm});
            skSolve(sketch);
        }
        {
            var Q0;
            Q0=qSketchRegion(id+"F29",true);
            extrude(context, id + "F30", {"entities" : qUnion([Q0]), "operationType" : NewBodyOperationType.REMOVE, "oppositeDirection" : true, "depth" : 7 * mm});
        }
        {
            var Q0;
            Q0=qCreatedBy(makeId("Right.planeOp"),FACE);
            var sketch = newSketch(context, id + "F31", { "sketchPlane" : qUnion([Q0])});
            skLineSegment(sketch, "E120.bottom", {"start": v(-37.5, 159.6) * mm, "end": v(-92.54, 159.6) * mm});
            skLineSegment(sketch, "E120.top", {"start": v(-37.5, -19.85) * mm, "end": v(-92.54, -19.85) * mm});
            skLineSegment(sketch, "E120.left", {"start": v(-37.5, 159.6) * mm, "end": v(-37.5, -19.85) * mm});
            skLineSegment(sketch, "E120.right", {"start": v(-92.54, 159.6) * mm, "end": v(-92.54, -19.85) * mm});
            skSolve(sketch);
        }
        {
            var Q0;
            Q0=qSketchRegion(id+"F31",true);
            extrude(context, id + "F32", {"entities" : qUnion([Q0]), "operationType" : NewBodyOperationType.REMOVE, "oppositeDirection" : true, "depth" : 197 * mm});
        }
        {
            var Q0;
            Q0=makeQuery(id+"F32.boolean.opBoolean","COPY",FACE,{"derivedFrom":makeQuery(id+"F32.opExtrude","SWEPT_FACE",FACE,{"disambiguationData":[OSD([sQuery(id+"F31.wireOp",EDGE,"E120.left")])]})});
            var sketch = newSketch(context, id + "F33", { "sketchPlane" : qUnion([Q0])});
            skLineSegment(sketch, "E121", {"start": v(-40.56, 72.5) * mm, "end": v(-109.44, 72.5) * mm});
            skCircle(sketch, "E122", {"center": v(-75, 72.5) * mm, "radius": 1.55 * mm});
            skLineSegment(sketch, "E123", {"start": v(-75, 123.57) * mm, "end": v(-75, -4.49) * mm, "construction": true});
            skSolve(sketch);
        }
        {
            var Q0;
            Q0=qSketchRegion(id+"F33",true);
            extrude(context, id + "F34", {"entities" : qUnion([Q0]), "operationType" : NewBodyOperationType.REMOVE, "oppositeDirection" : true, "depth" : 10 * mm});
        }
        {
            var Q0;
            {var subQ0=sQuery(id+"F22.wireOp",EDGE,"E63.left");Q0=makeQuery(id+"F30.boolean.opBoolean","INTERSECT",EDGE,{"derivedFrom":[makeQuery(id+"F28.boolean.opBoolean","MERGE",FACE,{"derivedFrom":[makeQuery(id+"F23.boolean.opBoolean","COPY",FACE,{"derivedFrom":makeQuery(id+"F23.opExtrude","CAP_FACE",FACE,{"disambiguationData":[OSD([sQuery(id+"F22.wireOp",EDGE,"E63.bottom"),sQuery(id+"F22.wireOp",EDGE,"E63.top"),subQ0,sQuery(id+"F22.wireOp",EDGE,"E69.bottom"),sQuery(id+"F22.wireOp",EDGE,"E69.top"),sQuery(id+"F22.wireOp",EDGE,"E71.bottom"),sQuery(id+"F22.wireOp",EDGE,"E71.top"),sQuery(id+"F22.wireOp",EDGE,"E72.left")])],"isStart":false})}),makeQuery(id+"F28.opExtrude","SWEPT_FACE",FACE,{"disambiguationData":[OSD([subQ0])]})]}),makeQuery(id+"F30.opExtrude","SWEPT_FACE",FACE,{"disambiguationData":[OSD([sQuery(id+"F29.wireOp",EDGE,"E115")])]})]});}
            fillet(context, id + "F35", {"entities" : qUnion([Q0]), "radius" : 5 * mm, "tangentPropagation" : true, "allowEdgeOverflow" : false});
        }
        {
            var Q0;
            {var subQ0=sQuery(id+"F22.wireOp",EDGE,"E63.left");Q0=makeQuery(id+"F35.opFillet","BLEND_EDGE",EDGE,{"blendedFrom":[makeQuery(id+"F30.boolean.opBoolean","INTERSECT",EDGE,{"derivedFrom":[makeQuery(id+"F28.boolean.opBoolean","MERGE",FACE,{"derivedFrom":[makeQuery(id+"F23.boolean.opBoolean","COPY",FACE,{"derivedFrom":makeQuery(id+"F23.opExtrude","CAP_FACE",FACE,{"disambiguationData":[OSD([sQuery(id+"F22.wireOp",EDGE,"E63.bottom"),sQuery(id+"F22.wireOp",EDGE,"E63.top"),subQ0,sQuery(id+"F22.wireOp",EDGE,"E69.bottom"),sQuery(id+"F22.wireOp",EDGE,"E69.top"),sQuery(id+"F22.wireOp",EDGE,"E71.bottom"),sQuery(id+"F22.wireOp",EDGE,"E71.top"),sQuery(id+"F22.wireOp",EDGE,"E72.left")])],"isStart":false})}),makeQuery(id+"F28.opExtrude","SWEPT_FACE",FACE,{"disambiguationData":[OSD([subQ0])]})]}),makeQuery(id+"F30.opExtrude","SWEPT_FACE",FACE,{"disambiguationData":[OSD([sQuery(id+"F29.wireOp",EDGE,"E115")])]})]}),makeQuery(id+"F28.boolean.opBoolean","COPY",FACE,{"derivedFrom":makeQuery(id+"F28.opExtrude","SWEPT_FACE",FACE,{"disambiguationData":[OSD([sQuery(id+"F27.wireOp",EDGE,"E113")])]})})],"blendedInto":[makeQuery(id+"F28.boolean.opBoolean","COPY",FACE,{"derivedFrom":makeQuery(id+"F28.opExtrude","SWEPT_FACE",FACE,{"disambiguationData":[OSD([sQuery(id+"F27.wireOp",EDGE,"E113")])]})})]});}
            fillet(context, id + "F51", {"entities" : qUnion([Q0]), "radius" : 5 * mm, "tangentPropagation" : true, "allowEdgeOverflow" : false});
        }
        {
            var Q0;
            Q0=makeQuery(id+"F7.boolean.opBoolean","COPY",FACE,{"derivedFrom":makeQuery(id+"F7.opExtrude","SWEPT_FACE",FACE,{"disambiguationData":[OSD([sQuery(id+"F6.wireOp",EDGE,"E19")])]})});
            var sketch = newSketch(context, id + "F36", { "sketchPlane" : qUnion([Q0])});
            skLineSegment(sketch, "E124.bottom", {"start": v(-37.5, 114.2) * mm, "end": v(-35, 114.2) * mm});
            skLineSegment(sketch, "E124.top", {"start": v(-37.5, 114.95) * mm, "end": v(-35, 114.95) * mm});
            skLineSegment(sketch, "E124.left", {"start": v(-37.5, 114.2) * mm, "end": v(-37.5, 114.95) * mm});
            skLineSegment(sketch, "E124.right", {"start": v(-35, 114.2) * mm, "end": v(-35, 114.95) * mm});
            skSolve(sketch);
        }
        {
            var Q0;
            Q0=qSketchRegion(id+"F36",true);
            extrude(context, id + "F37", {"entities" : qUnion([Q0]), "operationType" : NewBodyOperationType.REMOVE, "oppositeDirection" : true, "depth" : 25 * mm});
        }
        {
            var Q0;
            Q0=makeQuery(id+"F7.boolean.opBoolean","COPY",FACE,{"derivedFrom":makeQuery(id+"F7.opExtrude","SWEPT_FACE",FACE,{"disambiguationData":[OSD([sQuery(id+"F6.wireOp",EDGE,"E21")])]})});
            var sketch = newSketch(context, id + "F38", { "sketchPlane" : qUnion([Q0])});
            skLineSegment(sketch, "E125.bottom", {"start": v(37.5, 114.2) * mm, "end": v(35, 114.2) * mm});
            skLineSegment(sketch, "E125.top", {"start": v(37.5, 114.95) * mm, "end": v(35, 114.95) * mm});
            skLineSegment(sketch, "E125.left", {"start": v(37.5, 114.2) * mm, "end": v(37.5, 114.95) * mm});
            skLineSegment(sketch, "E125.right", {"start": v(35, 114.2) * mm, "end": v(35, 114.95) * mm});
            skSolve(sketch);
        }
        {
            var Q0;
            Q0=qSketchRegion(id+"F38",true);
            extrude(context, id + "F39", {"entities" : qUnion([Q0]), "operationType" : NewBodyOperationType.REMOVE, "oppositeDirection" : true, "depth" : 25 * mm});
        }
        {
            var Q0;
            Q0=makeQuery(id+"F1.opExtrude","CAP_FACE",FACE,{"disambiguationData":[OSD([sQuery(id+"F0.wireOp",EDGE,"E3")])],"isStart":false});
            var sketch = newSketch(context, id + "F40", { "sketchPlane" : qUnion([Q0])});
            skLineSegment(sketch, "E126", {"start": v(-75, -3.38) * mm, "end": v(-75, -37.5) * mm});
            skLineSegment(sketch, "E127", {"start": v(-106.11, -3.38) * mm, "end": v(-43.89, -3.38) * mm});
            skEllipticalArc(sketch, "E128.0", {});
            skPoint(sketch, "E129.orphan", {"position": v(-150, -37.5) * mm});
            skPoint(sketch, "E130.orphan", {"position": v(0, -37.5) * mm});
            skPoint(sketch, "E131.orphan", {"position": v(-75, 0) * mm});
            const initialGuessF40  = {"E128.0": [-0.075, -0.0375, 1, 0, 0.075, 0.0375, 1.1430642252800542, 1.9985284283097393]};
            skSetInitialGuess(sketch, initialGuessF40);
            skSolve(sketch);
        }
        {
            var Q0;
            {var subQ2=sQuery(id+"F40.wireOp",EDGE,"E128.0");Q0=makeQuery(id+"F40.imprint","IMPRINT",FACE,{"disambiguationData":[TD([[makeQuery(id+"F40.imprint","IMPRINT",EDGE,{"derivedFrom":subQ2}),1.0]])]});}
            extrude(context, id + "F41", {"entities" : qUnion([Q0]), "operationType" : NewBodyOperationType.REMOVE, "oppositeDirection" : true, "depth" : 152 * mm});
        }
        {
            var Q0;
            Q0=makeQuery(id+"F1.opExtrude","CAP_FACE",FACE,{"disambiguationData":[OSD([sQuery(id+"F0.wireOp",EDGE,"E3")])],"isStart":false});
            var sketch = newSketch(context, id + "F42", { "sketchPlane" : qUnion([Q0])});
            skLineSegment(sketch, "E132", {"start": v(-75, -37.5) * mm, "end": v(-75, -10.5) * mm});
            skLineSegment(sketch, "E133", {"start": v(-75, -10.5) * mm, "end": v(-64, -10.5) * mm});
            skLineSegment(sketch, "E134", {"start": v(-64, -10.5) * mm, "end": v(-64, -37.5) * mm});
            skLineSegment(sketch, "E135", {"start": v(-75, -10.5) * mm, "end": v(-86, -10.5) * mm});
            skLineSegment(sketch, "E136", {"start": v(-86, -10.5) * mm, "end": v(-86, -37.5) * mm});
            skLineSegment(sketch, "E137", {"start": v(-86, -37.5) * mm, "end": v(-64, -37.5) * mm});
            skLineSegment(sketch, "E138", {"start": v(-64, -10.5) * mm, "end": v(-64, -3.35) * mm});
            skLineSegment(sketch, "E139", {"start": v(-86, -10.5) * mm, "end": v(-86, -3.35) * mm});
            skLineSegment(sketch, "E140", {"start": v(-86, -3.35) * mm, "end": v(-64, -3.35) * mm});
            skCircle(sketch, "E141", {"center": v(-80.5, -6.94) * mm, "radius": 1.4 * mm});
            skCircle(sketch, "E142", {"center": v(-70.5, -6.94) * mm, "radius": 1.4 * mm});
            skLineSegment(sketch, "E143", {"start": v(-80.5, -6.94) * mm, "end": v(-70.5, -6.94) * mm, "construction": true});
            skLineSegment(sketch, "E144", {"start": v(-75.5, -6.94) * mm, "end": v(-75.5, -3.38) * mm});
            skSolve(sketch);
        }
        {
            var Q0;
            {var subQ0=sQuery(id+"F42.wireOp",EDGE,"E132");Q0=makeQuery(id+"F42.imprint","IMPRINT",FACE,{"disambiguationData":[TD([[makeQuery(id+"F42.imprint","IMPRINT",EDGE,{"derivedFrom":subQ0}),-1.0]])]});}
            var Q1;
            {var subQ0=sQuery(id+"F42.wireOp",EDGE,"E132");Q1=makeQuery(id+"F42.imprint","IMPRINT",FACE,{"disambiguationData":[TD([[makeQuery(id+"F42.imprint","IMPRINT",EDGE,{"derivedFrom":subQ0}),1.0]])]});}
            extrude(context, id + "F43", {"entities" : qUnion([Q0, Q1]), "operationType" : NewBodyOperationType.REMOVE, "oppositeDirection" : true, "depth" : 30 * mm});
        }
        {
            var Q0;
            Q0=makeQuery(id+"F42.imprint","IMPRINT",FACE,{"disambiguationData":[TD([[makeQuery(id+"F42.imprint","IMPRINT",EDGE,{"derivedFrom":sQuery(id+"F42.wireOp",EDGE,"E142")}),1.0]])]});
            var Q1;
            Q1=makeQuery(id+"F42.imprint","IMPRINT",FACE,{"disambiguationData":[TD([[makeQuery(id+"F42.imprint","IMPRINT",EDGE,{"derivedFrom":sQuery(id+"F42.wireOp",EDGE,"E141")}),1.0]])]});
            extrude(context, id + "F44", {"entities" : qUnion([Q0, Q1]), "operationType" : NewBodyOperationType.REMOVE, "oppositeDirection" : true, "depth" : 10 * mm});
        }
        {
            var Q0;
            Q0=makeQuery(id+"F41.boolean.opBoolean","COPY",FACE,{"derivedFrom":makeQuery(id+"F41.opExtrude","SWEPT_FACE",FACE,{"disambiguationData":[OSD([sQuery(id+"F40.wireOp",EDGE,"E127")])]})});
            var sketch = newSketch(context, id + "F45", { "sketchPlane" : qUnion([Q0])});
            skPoint(sketch, "E145", {"position": v(43.89, 62.5) * mm});
            skPoint(sketch, "E146", {"position": v(106.11, 62.5) * mm});
            skLineSegment(sketch, "E147", {"start": v(106.11, 62.5) * mm, "end": v(43.89, 62.5) * mm, "construction": true});
            skPoint(sketch, "E148", {"position": v(75, 62.5) * mm});
            skLineSegment(sketch, "E149.bottom", {"start": v(106.11, 93.61) * mm, "end": v(43.89, 93.61) * mm, "construction": true});
            skLineSegment(sketch, "E149.top", {"start": v(106.11, 31.39) * mm, "end": v(43.89, 31.39) * mm, "construction": true});
            skLineSegment(sketch, "E149.left", {"start": v(106.11, 93.61) * mm, "end": v(106.11, 31.39) * mm, "construction": true});
            skLineSegment(sketch, "E149.right", {"start": v(43.89, 93.61) * mm, "end": v(43.89, 31.39) * mm, "construction": true});
            skLineSegment(sketch, "E150", {"start": v(43.89, 82.2) * mm, "end": v(106.11, 82.2) * mm, "construction": true});
            skLineSegment(sketch, "E151", {"start": v(95.61, 33.52) * mm, "end": v(43.89, 33.52) * mm, "construction": true});
            skLineSegment(sketch, "E152", {"start": v(61.44, 75.4) * mm, "end": v(89.17, 75.4) * mm});
            skLineSegment(sketch, "E153", {"start": v(106.11, 62.5) * mm, "end": v(106.11, 33.52) * mm});
            skLineSegment(sketch, "E154", {"start": v(106.11, 48.01) * mm, "end": v(43.89, 48.01) * mm, "construction": true});
            skLineSegment(sketch, "E155", {"start": v(62.96, 62.5) * mm, "end": v(55.89, 48.01) * mm});
            skLineSegment(sketch, "E156", {"start": v(66.33, 69.4) * mm, "end": v(54.33, 69.4) * mm});
            skLineSegment(sketch, "E157", {"start": v(54.33, 69.4) * mm, "end": v(89.17, 69.4) * mm});
            skLineSegment(sketch, "E158", {"start": v(89.17, 75.4) * mm, "end": v(89.17, 69.4) * mm, "construction": true});
            skLineSegment(sketch, "E159", {"start": v(89.17, 62.5) * mm, "end": v(82.46, 62.5) * mm});
            skLineSegment(sketch, "E160", {"start": v(55.89, 82.2) * mm, "end": v(89.17, 82.2) * mm});
            skLineSegment(sketch, "E161", {"start": v(89.17, 82.2) * mm, "end": v(89.17, 62.5) * mm, "construction": true});
            skArc(sketch, "E162", {"start": v(89.17, 62.5) * mm, "mid": v(99.02, 72.35) * mm, "end": v(89.17, 82.2) * mm});
            skArc(sketch, "E163", {"start": v(89.17, 69.4) * mm, "mid": v(92.17, 72.4) * mm, "end": v(89.17, 75.4) * mm});
            skLineSegment(sketch, "E164.trimOffspring", {"start": v(82.46, 62.5) * mm, "end": v(103.33, 36.93) * mm});
            skLineSegment(sketch, "E165.trimOffspring", {"start": v(54.33, 69.4) * mm, "end": v(43.89, 48.01) * mm});
            skLineSegment(sketch, "E166.trimOffspring", {"start": v(71.96, 62.5) * mm, "end": v(92.83, 36.93) * mm});
            skLineSegment(sketch, "E167.trimOffspring", {"start": v(71.96, 62.5) * mm, "end": v(62.96, 62.5) * mm});
            skLineSegment(sketch, "E168", {"start": v(43.89, 48.01) * mm, "end": v(55.89, 48.01) * mm});
            skLineSegment(sketch, "E169", {"start": v(103.33, 36.93) * mm, "end": v(92.83, 36.93) * mm});
            skLineSegment(sketch, "E170", {"start": v(61.44, 75.4) * mm, "end": v(56.64, 75.4) * mm});
            skLineSegment(sketch, "E171", {"start": v(56.64, 75.4) * mm, "end": v(51.1, 82.2) * mm});
            skLineSegment(sketch, "E172", {"start": v(51.1, 82.2) * mm, "end": v(55.89, 82.2) * mm});
            skLineSegment(sketch, "E173", {"start": v(54.78, 80.45) * mm, "end": v(57.47, 77.15) * mm});
            skLineSegment(sketch, "E174", {"start": v(57.47, 77.15) * mm, "end": v(89.17, 77.15) * mm});
            skLineSegment(sketch, "E175", {"start": v(54.78, 80.45) * mm, "end": v(89.17, 80.45) * mm});
            skLineSegment(sketch, "E176", {"start": v(55.43, 67.65) * mm, "end": v(46.7, 49.76) * mm});
            skLineSegment(sketch, "E177", {"start": v(46.7, 49.76) * mm, "end": v(54.8, 49.76) * mm});
            skLineSegment(sketch, "E178", {"start": v(54.8, 49.76) * mm, "end": v(61.87, 64.25) * mm});
            skLineSegment(sketch, "E179", {"start": v(61.87, 64.25) * mm, "end": v(72.8, 64.25) * mm});
            skLineSegment(sketch, "E180", {"start": v(55.43, 67.65) * mm, "end": v(89.17, 67.65) * mm});
            skLineSegment(sketch, "E181", {"start": v(72.8, 64.25) * mm, "end": v(93.66, 38.68) * mm});
            skLineSegment(sketch, "E182", {"start": v(93.66, 38.68) * mm, "end": v(99.65, 38.68) * mm});
            skLineSegment(sketch, "E183", {"start": v(99.65, 38.68) * mm, "end": v(78.78, 64.25) * mm});
            skLineSegment(sketch, "E184.trimOffspring", {"start": v(78.78, 64.25) * mm, "end": v(89.17, 64.25) * mm});
            skArc(sketch, "E185", {"start": v(89.17, 67.65) * mm, "mid": v(93.92, 72.4) * mm, "end": v(89.17, 77.15) * mm});
            skArc(sketch, "E186", {"start": v(89.17, 64.25) * mm, "mid": v(97.27, 72.35) * mm, "end": v(89.17, 80.45) * mm});
            skSolve(sketch);
        }
        {
            var Q0;
            Q0=qSketchRegion(id+"F45",true);
            extrude(context, id + "F46", {"entities" : qUnion([Q0]), "operationType" : NewBodyOperationType.REMOVE, "oppositeDirection" : true, "depth" : 3 * mm});
        }
        {
            var Q0;
            Q0=makeQuery(id+"F1.opExtrude","CAP_FACE",FACE,{"disambiguationData":[OSD([sQuery(id+"F0.wireOp",EDGE,"E3")])],"isStart":true});
            var sketch = newSketch(context, id + "F47", { "sketchPlane" : qUnion([Q0])});
            skLineSegment(sketch, "E187.bottom", {"start": v(-19, 37.5) * mm, "end": v(-18.25, 37.5) * mm});
            skLineSegment(sketch, "E187.top", {"start": v(-19, 35) * mm, "end": v(-18.25, 35) * mm});
            skLineSegment(sketch, "E187.left", {"start": v(-19, 37.5) * mm, "end": v(-19, 35) * mm});
            skLineSegment(sketch, "E187.right", {"start": v(-18.25, 37.5) * mm, "end": v(-18.25, 35) * mm});
            skLineSegment(sketch, "E188.bottom", {"start": v(-131, 37.5) * mm, "end": v(-131.75, 37.5) * mm});
            skLineSegment(sketch, "E188.top", {"start": v(-131, 35) * mm, "end": v(-131.75, 35) * mm});
            skLineSegment(sketch, "E188.left", {"start": v(-131, 37.5) * mm, "end": v(-131, 35) * mm});
            skLineSegment(sketch, "E188.right", {"start": v(-131.75, 37.5) * mm, "end": v(-131.75, 35) * mm});
            skSolve(sketch);
        }
        {
            var Q0;
            Q0=qSketchRegion(id+"F47",true);
            extrude(context, id + "F48", {"entities" : qUnion([Q0]), "operationType" : NewBodyOperationType.REMOVE, "oppositeDirection" : true, "depth" : 1.8 * mm});
        }
        {
            var Q0;
            Q0=makeQuery(id+"F32.boolean.opBoolean","COPY",FACE,{"derivedFrom":makeQuery(id+"F32.opExtrude","SWEPT_FACE",FACE,{"disambiguationData":[OSD([sQuery(id+"F31.wireOp",EDGE,"E120.left")])]})});
            var sketch = newSketch(context, id + "F49", { "sketchPlane" : qUnion([Q0])});
            skLineSegment(sketch, "E189.bottom", {"start": v(-101.44, 87) * mm, "end": v(-48.56, 87) * mm});
            skLineSegment(sketch, "E189.left", {"start": v(-101.44, 87) * mm, "end": v(-101.44, 64.5) * mm});
            skLineSegment(sketch, "E189.right", {"start": v(-48.56, 87) * mm, "end": v(-48.56, 64.5) * mm});
            skLineSegment(sketch, "E190", {"start": v(-101.44, 64.5) * mm, "end": v(-123, 64.5) * mm});
            skLineSegment(sketch, "E191", {"start": v(-123, 64.5) * mm, "end": v(-123, 45.5) * mm});
            skLineSegment(sketch, "E192", {"start": v(-123, 45.5) * mm, "end": v(-81.3, 45.5) * mm});
            skLineSegment(sketch, "E193", {"start": v(-81.3, 45.5) * mm, "end": v(-81.3, 8) * mm});
            skLineSegment(sketch, "E194", {"start": v(-81.3, 8) * mm, "end": v(-68.7, 8) * mm});
            skLineSegment(sketch, "E195", {"start": v(-68.7, 8) * mm, "end": v(-68.7, 45.5) * mm});
            skLineSegment(sketch, "E196", {"start": v(-68.7, 45.5) * mm, "end": v(-27, 45.5) * mm});
            skLineSegment(sketch, "E197", {"start": v(-27, 45.5) * mm, "end": v(-27, 64.5) * mm});
            skLineSegment(sketch, "E198", {"start": v(-27, 64.5) * mm, "end": v(-48.56, 64.5) * mm});
            skSolve(sketch);
        }
        {
            var Q0;
            Q0 = qSketchRegion(id + "F49", true);
            extrude(context, id + "F50", {"entities" : qUnion([Q0]), "operationType" : NewBodyOperationType.REMOVE, "oppositeDirection" : true, "depth" : 20 * mm});
        }
    });
